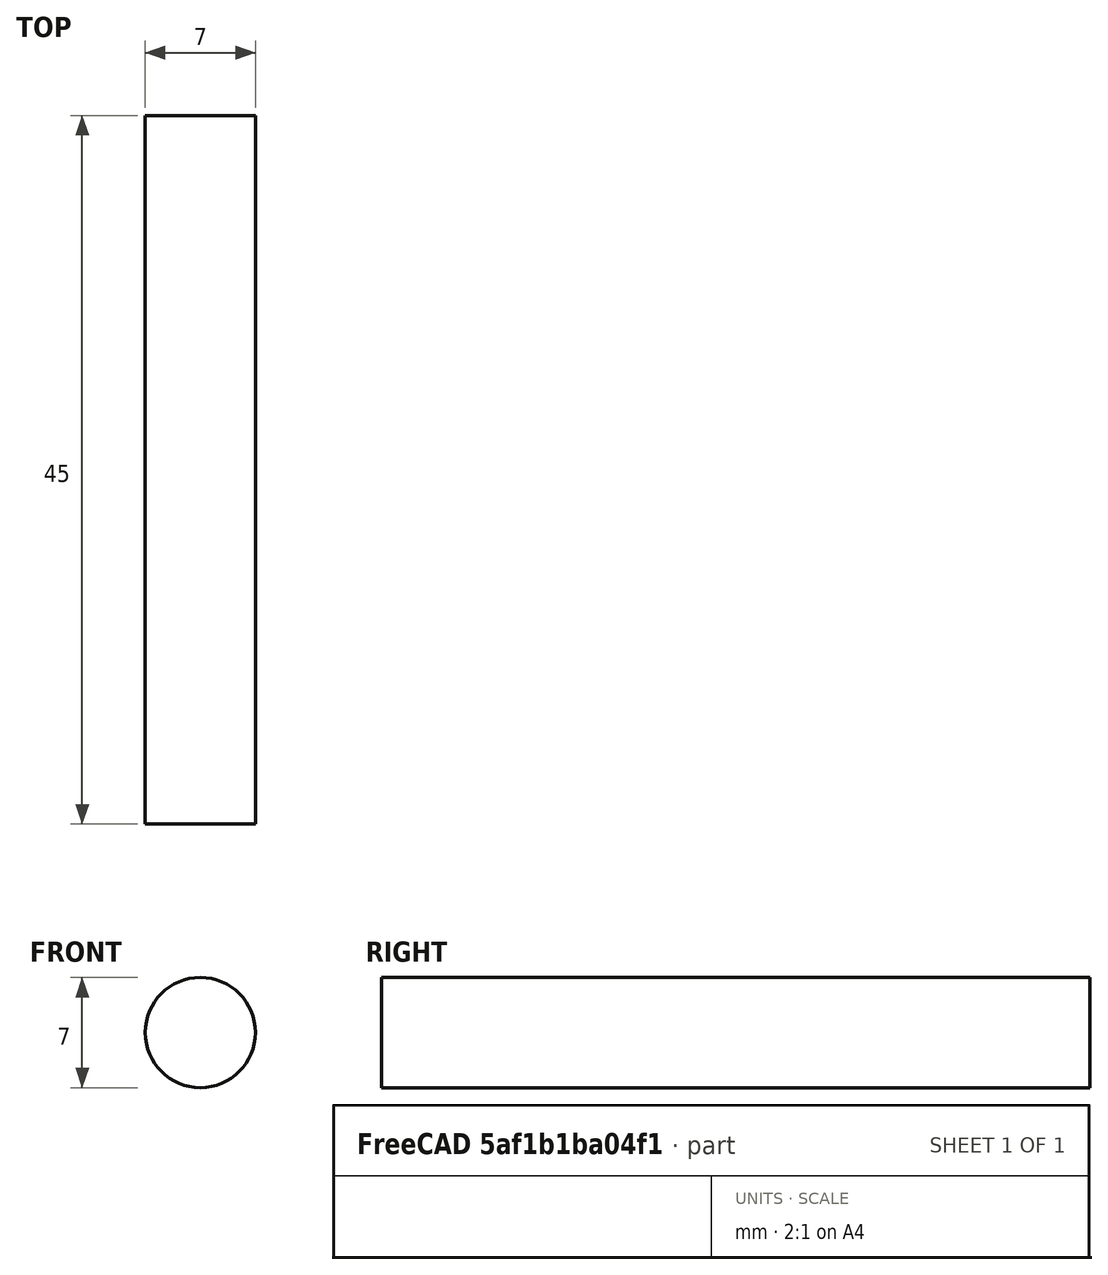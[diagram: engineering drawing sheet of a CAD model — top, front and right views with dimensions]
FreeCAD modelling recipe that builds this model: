
FCSTD DOCUMENT  (FreeCAD 0.21R33771 (Git))
Label: cutting tool
License: All rights reserved
LicenseURL: http://en.wikipedia.org/wiki/All_rights_reserved
objects: Sketcher::SketchObject×1, PartDesign::Pad×1, PartDesign::Body×1
note: 4 computed .brp shape members not serialized (recipe doc carries the construction recipe); baked Part::Feature solids carry a one-line shape summary decoded from their .brp

FEATURE [Sketcher::SketchObject] Sketch
  FullyConstrained = true
  MapMode = 5
  Placement = pos=(0,0,0) rot=(1,0,0;1.5708rad)
  Support = -> [XZ_Plane]
  sketch-geometry (1):
    g0: Circle CenterX=0 CenterY=0 CenterZ=0 NormalX=0 NormalY=0 NormalZ=1 AngleXU=0 Radius=3.5
  constraints (2):
    c: Coincident(g0,g-1)
    c: Radius(g0) = 3.5
FEATURE [PartDesign::Pad] Pad
  Direction = (0,-1,2e-16)
  Length = 45
  Length2 = 10
  Placement = pos=(0,0,0) rot=(1,0,0;1.5708rad)
  Profile = -> Sketch
  ReferenceAxis = -> Sketch [N_Axis]
  Type = 0
FEATURE [PartDesign::Body] Body
  Group = -> [Sketch,Pad]
  Origin = -> Origin
  Tip = -> Pad
